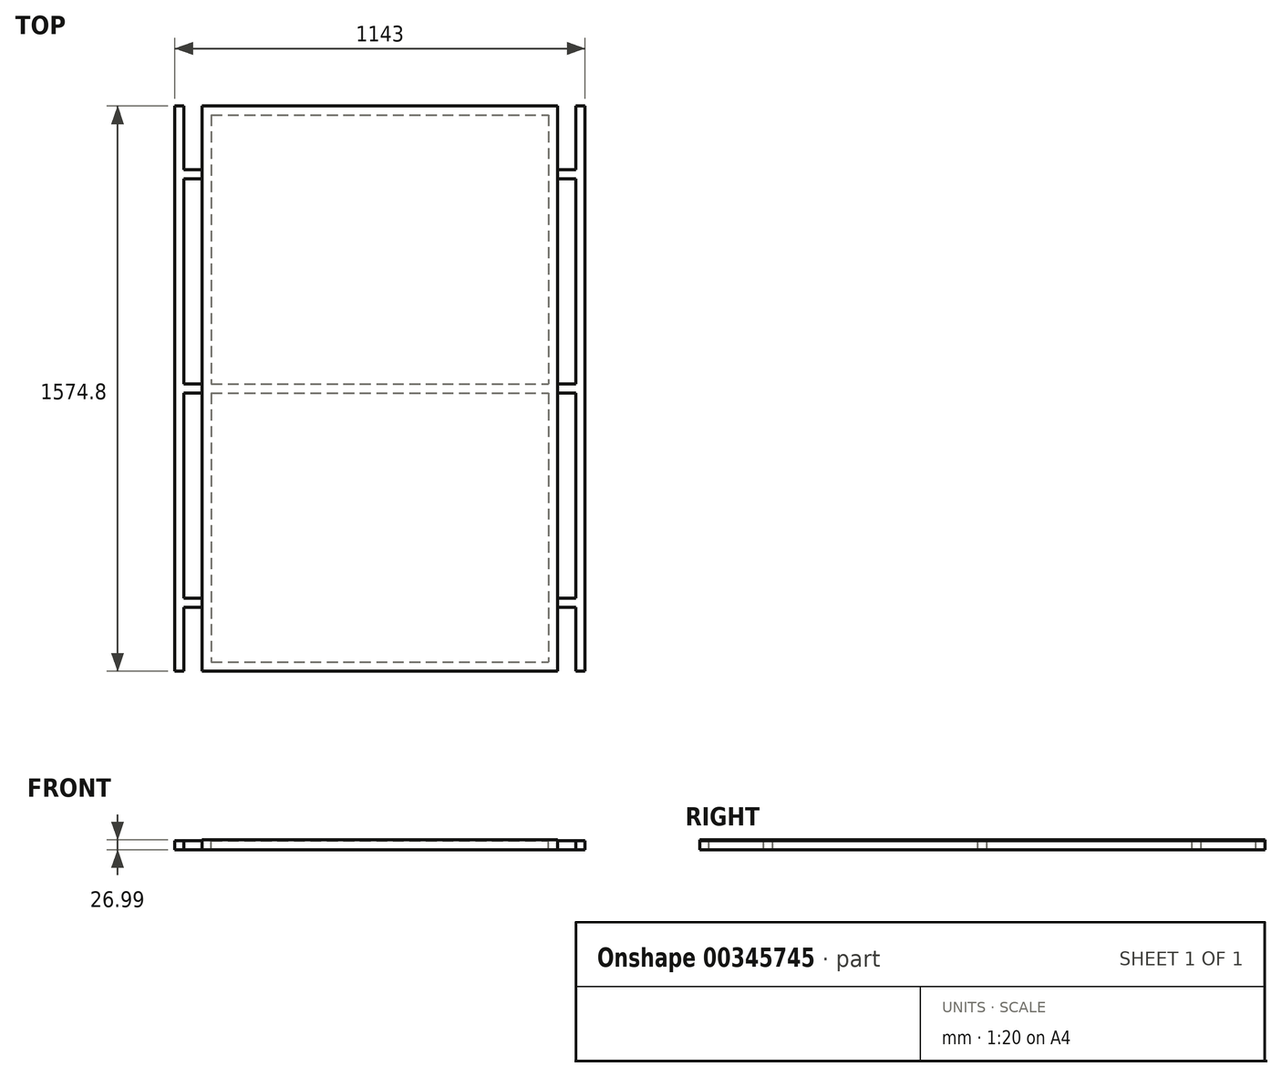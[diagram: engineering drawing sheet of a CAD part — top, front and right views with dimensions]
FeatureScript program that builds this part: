
annotation { "Feature Type Name" : "Feature", "Feature Type Description" : "" }
export const myFeature = defineFeature(function(context is Context, id is Id, definition is map)
    precondition{}
    {
        {
            var Q0;
            Q0=qCreatedBy(makeId("Top.planeOp"),FACE);
            var sketch = newSketch(context, id + "F0", { "sketchPlane" : qUnion([Q0])});
            skLineSegment(sketch, "E0.bottom", {"start": v(0, 0) * mm, "end": v(990.6, 0) * mm});
            skLineSegment(sketch, "E0.top", {"start": v(0, -1574.8) * mm, "end": v(990.6, -1574.8) * mm});
            skLineSegment(sketch, "E0.left", {"start": v(0, 0) * mm, "end": v(0, -1574.8) * mm});
            skLineSegment(sketch, "E0.right", {"start": v(990.6, 0) * mm, "end": v(990.6, -1574.8) * mm});
            skSolve(sketch);
        }
        {
            var Q0;
            Q0=makeQuery(id+"F0.imprint","IMPRINT",FACE,{"disambiguationData":[TD([[makeQuery(id+"F0.imprint","IMPRINT",EDGE,{"derivedFrom":sQuery(id+"F0.wireOp",EDGE,"E0.bottom")}),-1.0]])]});
            extrude(context, id + "F1", {"entities" : qUnion([Q0]), "depth" : 1.59 * mm});
        }
        {
            var Q0;
            Q0=makeQuery(id+"F1.opExtrude","CAP_FACE",FACE,{"disambiguationData":[OSD([sQuery(id+"F0.wireOp",EDGE,"E0.bottom"),sQuery(id+"F0.wireOp",EDGE,"E0.top"),sQuery(id+"F0.wireOp",EDGE,"E0.left"),sQuery(id+"F0.wireOp",EDGE,"E0.right")])],"isStart":true});
            var sketch = newSketch(context, id + "F2", { "sketchPlane" : qUnion([Q0])});
            skLineSegment(sketch, "E1.bottom", {"start": v(25.4, 25.4) * mm, "end": v(965.2, 25.4) * mm});
            skLineSegment(sketch, "E1.top", {"start": v(25.4, 774.7) * mm, "end": v(965.2, 774.7) * mm});
            skLineSegment(sketch, "E1.left", {"start": v(25.4, 25.4) * mm, "end": v(25.4, 774.7) * mm});
            skLineSegment(sketch, "E1.right", {"start": v(965.2, 25.4) * mm, "end": v(965.2, 774.7) * mm});
            skLineSegment(sketch, "E2.bottom", {"start": v(25.4, 800.1) * mm, "end": v(965.2, 800.1) * mm});
            skLineSegment(sketch, "E2.top", {"start": v(25.4, 1549.4) * mm, "end": v(965.2, 1549.4) * mm});
            skLineSegment(sketch, "E2.left", {"start": v(25.4, 800.1) * mm, "end": v(25.4, 1549.4) * mm});
            skLineSegment(sketch, "E2.right", {"start": v(965.2, 800.1) * mm, "end": v(965.2, 1549.4) * mm});
            skLineSegment(sketch, "E3.bottom", {"start": v(0, 0) * mm, "end": v(990.6, 0) * mm});
            skLineSegment(sketch, "E3.top", {"start": v(0, 1574.8) * mm, "end": v(990.6, 1574.8) * mm});
            skLineSegment(sketch, "E3.left", {"start": v(0, 0) * mm, "end": v(0, 1574.8) * mm});
            skLineSegment(sketch, "E3.right", {"start": v(990.6, 0) * mm, "end": v(990.6, 1574.8) * mm});
            skSolve(sketch);
        }
        {
            var Q0;
            Q0 = qSketchRegion(id + "F2", true);
            extrude(context, id + "F3", {"entities" : qUnion([Q0]), "operationType" : NewBodyOperationType.ADD, "depth" : 25.4 * mm});
        }
        {
            var Q0;
            Q0=makeQuery(id+"F3.boolean.opBoolean","MERGE",FACE,{"derivedFrom":[makeQuery(id+"F1.opExtrude","SWEPT_FACE",FACE,{"disambiguationData":[OSD([sQuery(id+"F0.wireOp",EDGE,"E0.left")])]}),makeQuery(id+"F3.opExtrude","SWEPT_FACE",FACE,{"disambiguationData":[OSD([sQuery(id+"F2.wireOp",EDGE,"E3.left")])]})]});
            var sketch = newSketch(context, id + "F4", { "sketchPlane" : qUnion([Q0])});
            skLineSegment(sketch, "E4.bottom", {"start": v(177.8, -25.4) * mm, "end": v(203.2, -25.4) * mm});
            skLineSegment(sketch, "E4.top", {"start": v(177.8, 0) * mm, "end": v(203.2, 0) * mm});
            skLineSegment(sketch, "E4.left", {"start": v(177.8, -25.4) * mm, "end": v(177.8, 0) * mm});
            skLineSegment(sketch, "E4.right", {"start": v(203.2, -25.4) * mm, "end": v(203.2, 0) * mm});
            skLineSegment(sketch, "E5.bottom", {"start": v(774.7, -25.4) * mm, "end": v(800.1, -25.4) * mm});
            skLineSegment(sketch, "E5.top", {"start": v(774.7, 0) * mm, "end": v(800.1, 0) * mm});
            skLineSegment(sketch, "E5.left", {"start": v(774.7, -25.4) * mm, "end": v(774.7, 0) * mm});
            skLineSegment(sketch, "E5.right", {"start": v(800.1, -25.4) * mm, "end": v(800.1, 0) * mm});
            skLineSegment(sketch, "E6.bottom", {"start": v(1371.6, -25.4) * mm, "end": v(1397, -25.4) * mm});
            skLineSegment(sketch, "E6.top", {"start": v(1371.6, 0) * mm, "end": v(1397, 0) * mm});
            skLineSegment(sketch, "E6.left", {"start": v(1371.6, -25.4) * mm, "end": v(1371.6, 0) * mm});
            skLineSegment(sketch, "E6.right", {"start": v(1397, -25.4) * mm, "end": v(1397, 0) * mm});
            skSolve(sketch);
        }
        {
            var Q0;
            Q0 = qSketchRegion(id + "F4", true);
            extrude(context, id + "F5", {"entities" : qUnion([Q0]), "operationType" : NewBodyOperationType.ADD, "depth" : 50.8 * mm});
        }
        {
            var Q0;
            Q0=makeQuery(id+"F3.boolean.opBoolean","MERGE",FACE,{"derivedFrom":[makeQuery(id+"F1.opExtrude","SWEPT_FACE",FACE,{"disambiguationData":[OSD([sQuery(id+"F0.wireOp",EDGE,"E0.bottom")])]}),makeQuery(id+"F3.opExtrude","SWEPT_FACE",FACE,{"disambiguationData":[OSD([sQuery(id+"F2.wireOp",EDGE,"E3.bottom")])]})]});
            var sketch = newSketch(context, id + "F6", { "sketchPlane" : qUnion([Q0])});
            skLineSegment(sketch, "E7.bottom", {"start": v(50.8, 0) * mm, "end": v(76.2, 0) * mm});
            skLineSegment(sketch, "E7.top", {"start": v(50.8, -25.4) * mm, "end": v(76.2, -25.4) * mm});
            skLineSegment(sketch, "E7.left", {"start": v(50.8, 0) * mm, "end": v(50.8, -25.4) * mm});
            skLineSegment(sketch, "E7.right", {"start": v(76.2, 0) * mm, "end": v(76.2, -25.4) * mm});
            skSolve(sketch);
        }
        {
            var Q0;
            Q0=makeQuery(id+"F6.imprint","IMPRINT",FACE,{"disambiguationData":[TD([[makeQuery(id+"F6.imprint","IMPRINT",EDGE,{"derivedFrom":sQuery(id+"F6.wireOp",EDGE,"E7.bottom")}),-1.0]])]});
            extrude(context, id + "F7", {"entities" : qUnion([Q0]), "operationType" : NewBodyOperationType.ADD, "oppositeDirection" : true, "depth" : 1574.8 * mm});
        }
        {
            var Q0;
            Q0=makeQuery(id+"F3.boolean.opBoolean","MERGE",FACE,{"derivedFrom":[makeQuery(id+"F1.opExtrude","SWEPT_FACE",FACE,{"disambiguationData":[OSD([sQuery(id+"F0.wireOp",EDGE,"E0.right")])]}),makeQuery(id+"F3.opExtrude","SWEPT_FACE",FACE,{"disambiguationData":[OSD([sQuery(id+"F2.wireOp",EDGE,"E3.right")])]})]});
            var sketch = newSketch(context, id + "F8", { "sketchPlane" : qUnion([Q0])});
            skLineSegment(sketch, "E8.bottom", {"start": v(-1397, -25.4) * mm, "end": v(-1371.6, -25.4) * mm});
            skLineSegment(sketch, "E8.top", {"start": v(-1397, 0) * mm, "end": v(-1371.6, 0) * mm});
            skLineSegment(sketch, "E8.left", {"start": v(-1397, -25.4) * mm, "end": v(-1397, 0) * mm});
            skLineSegment(sketch, "E8.right", {"start": v(-1371.6, -25.4) * mm, "end": v(-1371.6, 0) * mm});
            skLineSegment(sketch, "E9.bottom", {"start": v(-800.1, -25.4) * mm, "end": v(-774.7, -25.4) * mm});
            skLineSegment(sketch, "E9.top", {"start": v(-800.1, 0) * mm, "end": v(-774.7, 0) * mm});
            skLineSegment(sketch, "E9.left", {"start": v(-800.1, -25.4) * mm, "end": v(-800.1, 0) * mm});
            skLineSegment(sketch, "E9.right", {"start": v(-774.7, -25.4) * mm, "end": v(-774.7, 0) * mm});
            skLineSegment(sketch, "E10.bottom", {"start": v(-203.2, -25.4) * mm, "end": v(-177.8, -25.4) * mm});
            skLineSegment(sketch, "E10.top", {"start": v(-203.2, 0) * mm, "end": v(-177.8, 0) * mm});
            skLineSegment(sketch, "E10.left", {"start": v(-203.2, -25.4) * mm, "end": v(-203.2, 0) * mm});
            skLineSegment(sketch, "E10.right", {"start": v(-177.8, -25.4) * mm, "end": v(-177.8, 0) * mm});
            skSolve(sketch);
        }
        {
            var Q0;
            Q0 = qSketchRegion(id + "F8", true);
            extrude(context, id + "F9", {"entities" : qUnion([Q0]), "operationType" : NewBodyOperationType.ADD, "depth" : 50.8 * mm});
        }
        {
            var Q0;
            Q0=makeQuery(id+"F3.boolean.opBoolean","MERGE",FACE,{"derivedFrom":[makeQuery(id+"F1.opExtrude","SWEPT_FACE",FACE,{"disambiguationData":[OSD([sQuery(id+"F0.wireOp",EDGE,"E0.bottom")])]}),makeQuery(id+"F3.opExtrude","SWEPT_FACE",FACE,{"disambiguationData":[OSD([sQuery(id+"F2.wireOp",EDGE,"E3.bottom")])]})]});
            var sketch = newSketch(context, id + "F10", { "sketchPlane" : qUnion([Q0])});
            skLineSegment(sketch, "E11.bottom", {"start": v(-1041.4, 0) * mm, "end": v(-1066.8, 0) * mm});
            skLineSegment(sketch, "E11.top", {"start": v(-1041.4, -25.4) * mm, "end": v(-1066.8, -25.4) * mm});
            skLineSegment(sketch, "E11.left", {"start": v(-1041.4, 0) * mm, "end": v(-1041.4, -25.4) * mm});
            skLineSegment(sketch, "E11.right", {"start": v(-1066.8, 0) * mm, "end": v(-1066.8, -25.4) * mm});
            skSolve(sketch);
        }
        {
            var Q0;
            Q0 = qSketchRegion(id + "F10", true);
            extrude(context, id + "F11", {"entities" : qUnion([Q0]), "operationType" : NewBodyOperationType.ADD, "oppositeDirection" : true, "depth" : 1574.8 * mm});
        }
    });
